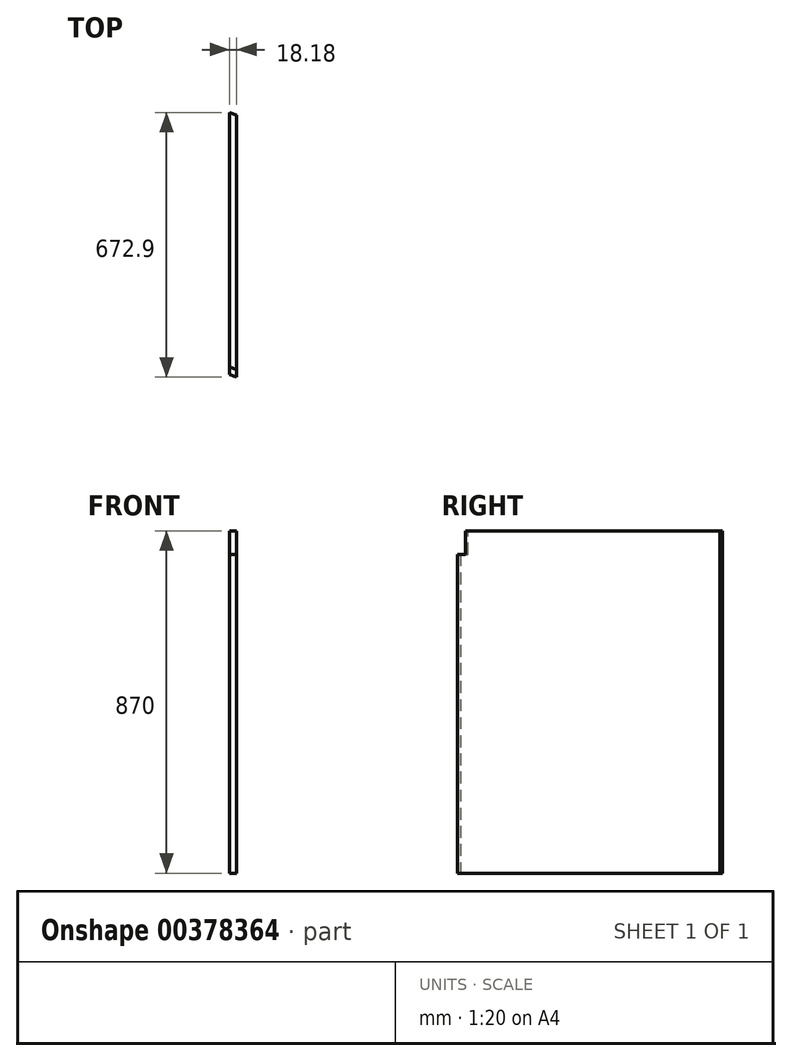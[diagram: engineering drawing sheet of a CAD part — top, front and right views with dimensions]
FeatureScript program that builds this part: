
annotation { "Feature Type Name" : "Feature", "Feature Type Description" : "" }
export const myFeature = defineFeature(function(context is Context, id is Id, definition is map)
    precondition{}
    {
        {
            var Q0;
            Q0=qCreatedBy(makeId("Top.planeOp"),FACE);
            var sketch = newSketch(context, id + "F0", { "sketchPlane" : qUnion([Q0])});
            skLineSegment(sketch, "E0.left", {"start": v(-9.1, 336.45) * mm, "end": v(-8.9, -329.55) * mm});
            skLineSegment(sketch, "E0.right", {"start": v(8.9, 329.55) * mm, "end": v(9.1, -336.45) * mm});
            skPoint(sketch, "E0.middle", {"position": v(0, 0) * mm});
            skLineSegment(sketch, "E1", {"start": v(-9.1, 336.45) * mm, "end": v(8.9, 329.55) * mm});
            skLineSegment(sketch, "E2", {"start": v(9.1, -336.45) * mm, "end": v(-8.9, -329.55) * mm});
            skSolve(sketch);
        }
        {
            var Q0;
            Q0=qSketchRegion(id+"F0",true);
            extrude(context, id + "F1", {"entities" : qUnion([Q0]), "depth" : 870 * mm});
        }
        {
            var Q0;
            Q0=makeQuery(id+"F1.opExtrude","CAP_FACE",FACE,{"disambiguationData":[OSD([sQuery(id+"F0.wireOp",EDGE,"E0.left"),sQuery(id+"F0.wireOp",EDGE,"E0.right"),sQuery(id+"F0.wireOp",EDGE,"E1"),sQuery(id+"F0.wireOp",EDGE,"E2")])],"isStart":false});
            var sketch = newSketch(context, id + "F2", { "sketchPlane" : qUnion([Q0])});
            skLineSegment(sketch, "E3", {"start": v(9.1, -336.45) * mm, "end": v(9.09, -317.17) * mm});
            skLineSegment(sketch, "E4", {"start": v(9.09, -317.17) * mm, "end": v(-8.91, -310.27) * mm});
            skLineSegment(sketch, "E5", {"start": v(-8.91, -310.27) * mm, "end": v(-8.9, -329.55) * mm});
            skLineSegment(sketch, "E6", {"start": v(-8.9, -329.55) * mm, "end": v(9.1, -336.45) * mm});
            skSolve(sketch);
        }
        {
            var Q0;
            Q0=qSketchRegion(id+"F2",true);
            extrude(context, id + "F3", {"entities" : qUnion([Q0]), "operationType" : NewBodyOperationType.REMOVE, "oppositeDirection" : true, "depth" : 60 * mm});
        }
    });
